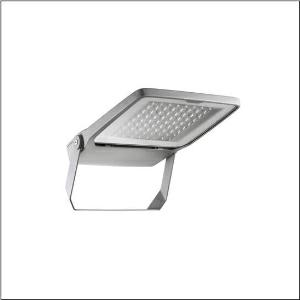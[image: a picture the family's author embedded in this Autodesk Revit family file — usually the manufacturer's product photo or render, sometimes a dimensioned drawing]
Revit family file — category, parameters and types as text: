
# Revit family: floodlight_fl_20_mini___pl52_5xa7672b1d1ac_ec5c
name_source: partatom
category: Lighting Fixtures
units: mm (PartAtom-declared; Revit-internal decimal feet)

## family parameters
Cut with Voids When Loaded = No
Host = Face
Light Source = No
Part Type = Normal
Room Calculation Point = No
Round Connector Dimension = Use Diameter
Shared = No

## types (1)
- --- (1 x LED 3000K / CRI = 80 (unbekannt), 4930 lm, 3000K)
    Apparent Load = 51 VA
    CIE Flux Codes = 27 59 98 100 100
    Color Rendering = 80
    Color Temperature = 3000K
    Default Elevation = 1800 mm
    Description = Floodlight FL 20 mini, floodlight, primary light control with lens, of plastic, primary optical cover: protective disc, of toughened safety glass, transparent, light distribution: PL52, light emission: direct distribution, primary light characteristic: asymmetric, installation type: surface-mounted, LED, High Power LED, rated luminous flux: 4.930lm, luminous efficacy: 97lm/W, light colour: 830, colour temperature: 3000K, control gear: ECG Plus, control: flexible luminous flux parameterisation, time-dependent luminous flux control, digital communication interface, power reduction, overheat protection, electronic power reduction, with terminal, 5-pole, max. 2.5mm², mains connection: 220..240V, AC, 50/60Hz, rated input power: 51W, LED unit, of diecast aluminium, powder-coated, Siteco® metallic grey (DB 702S), corrosivity category C5 mid according to DIN EN ISO 12944, incl. 1x M20 cable gland for cable Ø 6.5..12mm, length: 446mm, width: 355mm, height: 62mm, housing frame, of diecast aluminium, powder-coated, Siteco® metallic grey (DB 702S), mounting bracket, of steel, powder-coated, Siteco® metallic grey (DB 702S), DALI, protection rating (complete): IP66, insulation class (complete): insulation class II (safety insulation), certification: CE, ENEC, VDE, protection symbol: D, permissible operating ambient temperature: -40..+40°C, permissible operating ambient temperature for outdoor applications: -40..+50°C, standard: DIN EN 12944, packaging unit: 1 piece

Light Distribution: PL52
    Height = 62 mm  [stored 0.203412 ft]
    Lamp = 1 x LED 3000K / CRI >= 80 (unbekannt)
    Lamp Light Flux = 4930 lm
    Lamp count = 1
    Length = 467 mm
    Luminous efficacy = 97 lm/W
    Manufacturer = Siteco
    ModVariant = No
    Model = 5XA7672B1D1AC
    Mounting Place = Wall
    Mounting Type = Surface mounted
    Number of Poles = 1
    OnlyDefault = Yes
    Power Factor = 1
    Product Name = Floodlight FL 20 mini | PL52
    Product group = floodlight | wall mounted
    ProductGroupID = 2001
    Protection Class = Protection class II
    Protection Degree = IP 66
    RLX_Detail_Level = 1
    RLX_Emergency_Light_Flux = 0 lm
    RLX_Emergency_Type = 0
    RLX_Emergency_Type_DB = No
    RlxData = <blob elided: 74265 chars, md5=3000834f>
    Socket = socket
    Standby Power = 0 W
    System Light Flux = 4930 lm
    System Power = 51 W
    Type Comments = factory setting: luminous flux: 100 % | dim-lin: 254 | 520 mA
    Type Image = l_1005948.jpg
    URL = http://relux.com
    VarID = @adj_163993
    Voltage = 0 V
    Weight = 0.00 kg
    Width = 335 mm

note: [stored X ft] marks values corroborated as IEEE doubles in the binary element streams (Revit-internal decimal feet)

## geometry (parser evidence)
native form markers: Blend x4, Sweep x12
no freeform markers — native parametric forms only
